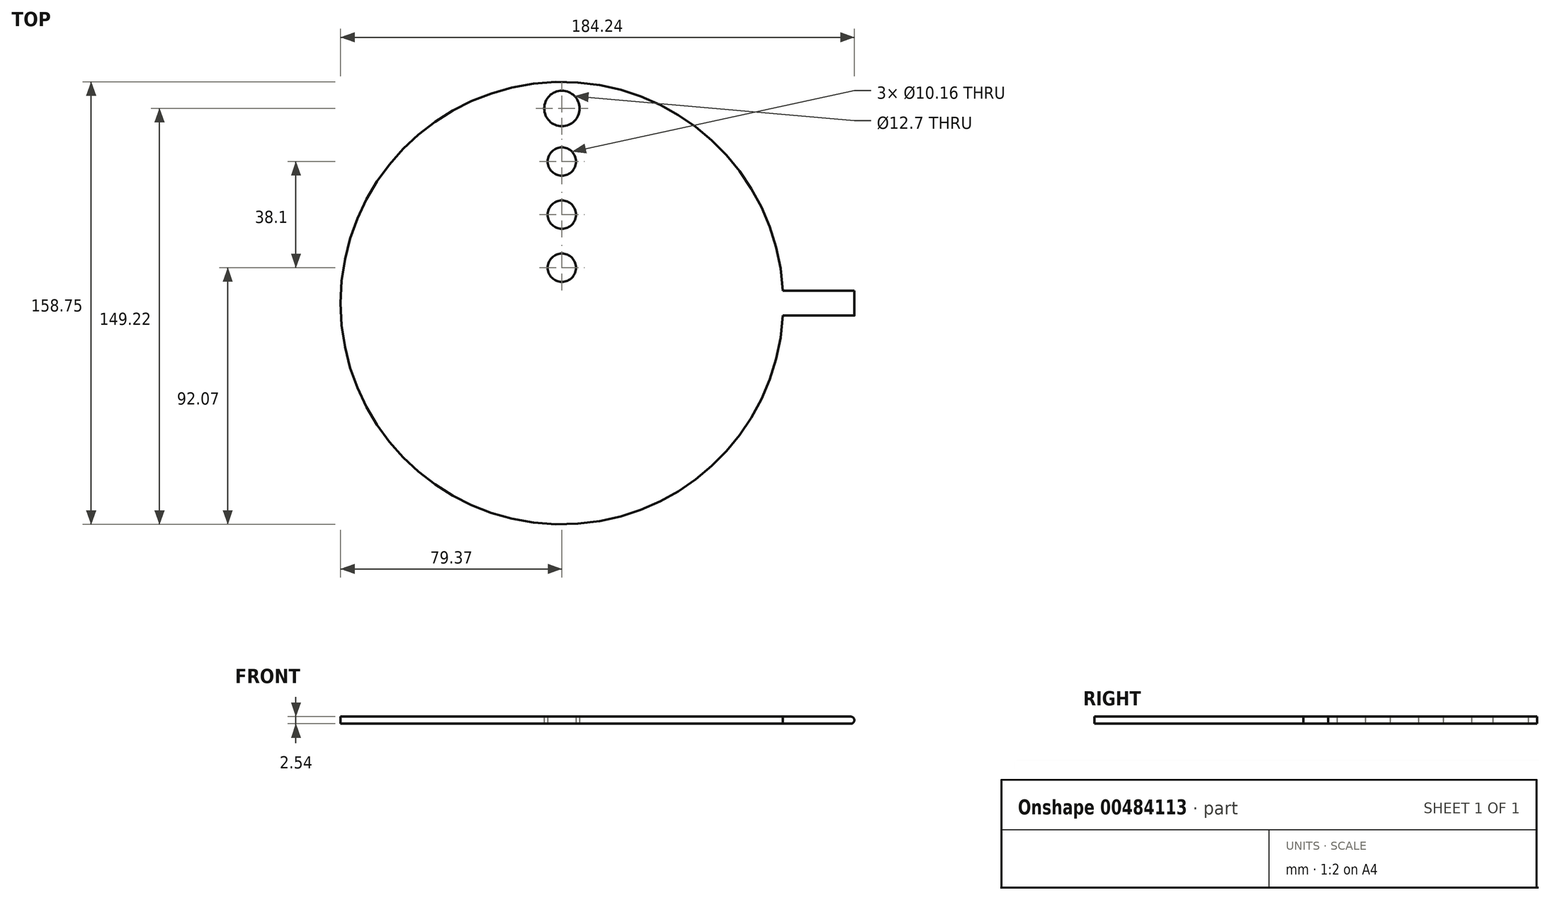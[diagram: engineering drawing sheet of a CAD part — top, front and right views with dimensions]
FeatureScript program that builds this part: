
annotation { "Feature Type Name" : "Feature", "Feature Type Description" : "" }
export const myFeature = defineFeature(function(context is Context, id is Id, definition is map)
    precondition{}
    {
        {
            var Q0;
            Q0=qCreatedBy(makeId("Top.planeOp"),FACE);
            var sketch = newSketch(context, id + "F0", { "sketchPlane" : qUnion([Q0])});
            skCircle(sketch, "E0", {"center": v(0, 0) * mm, "radius": 79.38 * mm});
            skLineSegment(sketch, "E1.bottom", {"start": v(79.25, 4.47) * mm, "end": v(104.87, 4.47) * mm});
            skLineSegment(sketch, "E1.top", {"start": v(79.25, -4.47) * mm, "end": v(104.87, -4.47) * mm});
            skLineSegment(sketch, "E1.left", {"start": v(79.25, 4.47) * mm, "end": v(79.25, -4.47) * mm});
            skLineSegment(sketch, "E1.right", {"start": v(104.87, 4.47) * mm, "end": v(104.87, -4.47) * mm});
            skPoint(sketch, "E1.middle", {"position": v(92.06, 0) * mm});
            skSolve(sketch);
        }
        {
            var Q0;
            Q0 = qSketchRegion(id + "F0", true);
            extrude(context, id + "F1", {"entities" : qUnion([Q0]), "depth" : 2.54 * mm});
        }
        {
            var Q0;
            Q0=qCreatedBy(makeId("Top.planeOp"),FACE);
            var sketch = newSketch(context, id + "F2", { "sketchPlane" : qUnion([Q0])});
            skLineSegment(sketch, "E2", {"start": v(0, 0) * mm, "end": v(0, 12.7) * mm, "construction": true});
            skCircle(sketch, "E3", {"center": v(0, 12.7) * mm, "radius": 5.08 * mm});
            skSolve(sketch);
        }
        {
            var Q0;
            Q0=qCreatedBy(makeId("Top.planeOp"),FACE);
            var sketch = newSketch(context, id + "F3", { "sketchPlane" : qUnion([Q0])});
            skLineSegment(sketch, "E4", {"start": v(0, 0) * mm, "end": v(0, 31.75) * mm, "construction": true});
            skCircle(sketch, "E5", {"center": v(0, 31.75) * mm, "radius": 5.08 * mm});
            skSolve(sketch);
        }
        {
            var Q0;
            Q0=qCreatedBy(makeId("Top.planeOp"),FACE);
            var sketch = newSketch(context, id + "F4", { "sketchPlane" : qUnion([Q0])});
            skLineSegment(sketch, "E6", {"start": v(0, 0) * mm, "end": v(0, 50.8) * mm, "construction": true});
            skCircle(sketch, "E7", {"center": v(0, 50.8) * mm, "radius": 5.08 * mm});
            skSolve(sketch);
        }
        {
            var Q0;
            Q0 = qSketchRegion(id + "F4", true);
            extrude(context, id + "F5", {"entities" : qUnion([Q0]), "operationType" : NewBodyOperationType.REMOVE, "depth" : 25.4 * mm});
        }
        {
            var Q0;
            Q0=qCreatedBy(makeId("Top.planeOp"),FACE);
            var sketch = newSketch(context, id + "F6", { "sketchPlane" : qUnion([Q0])});
            skLineSegment(sketch, "E8", {"start": v(0, 0) * mm, "end": v(0, 69.85) * mm, "construction": true});
            skCircle(sketch, "E9", {"center": v(0, 69.85) * mm, "radius": 6.35 * mm});
            skSolve(sketch);
        }
        {
            var Q0;
            Q0=makeQuery(id+"F1.opExtrude","CAP_FACE",FACE,{"disambiguationData":[OSD([sQuery(id+"F0.wireOp",EDGE,"E0"),sQuery(id+"F0.wireOp",EDGE,"E1.bottom"),sQuery(id+"F0.wireOp",EDGE,"E1.top"),sQuery(id+"F0.wireOp",EDGE,"E1.right")])],"isStart":false});
            var sketch = newSketch(context, id + "F7", { "sketchPlane" : qUnion([Q0])});
            skCircle(sketch, "E10", {"center": v(0, 0) * mm, "radius": 88.9 * mm, "construction": true});
            skSolve(sketch);
        }
        {
            var Q0;
            Q0 = qSketchRegion(id + "F6", true);
            extrude(context, id + "F8", {"entities" : qUnion([Q0]), "operationType" : NewBodyOperationType.REMOVE, "depth" : 25.4 * mm});
        }
        {
            var Q0;
            Q0 = qSketchRegion(id + "F3", true);
            extrude(context, id + "F9", {"entities" : qUnion([Q0]), "operationType" : NewBodyOperationType.REMOVE, "depth" : 25.4 * mm});
        }
        {
            var Q0;
            Q0 = qSketchRegion(id + "F2", true);
            extrude(context, id + "F10", {"entities" : qUnion([Q0]), "operationType" : NewBodyOperationType.REMOVE, "depth" : 25.4 * mm});
        }
        {
            var Q0;
            Q0=makeQuery(id+"F1.opExtrude","CAP_EDGE",EDGE,{"disambiguationData":[OSD([sQuery(id+"F0.wireOp",EDGE,"E1.right")])],"isStart":true});
            var Q1;
            Q1=makeQuery(id+"F1.opExtrude","CAP_EDGE",EDGE,{"disambiguationData":[OSD([sQuery(id+"F0.wireOp",EDGE,"E1.right")])],"isStart":false});
            fillet(context, id + "F11", {"entities" : qUnion([Q0, Q1]), "radius" : 1.27 * mm, "tangentPropagation" : true, "allowEdgeOverflow" : false});
        }
    });
